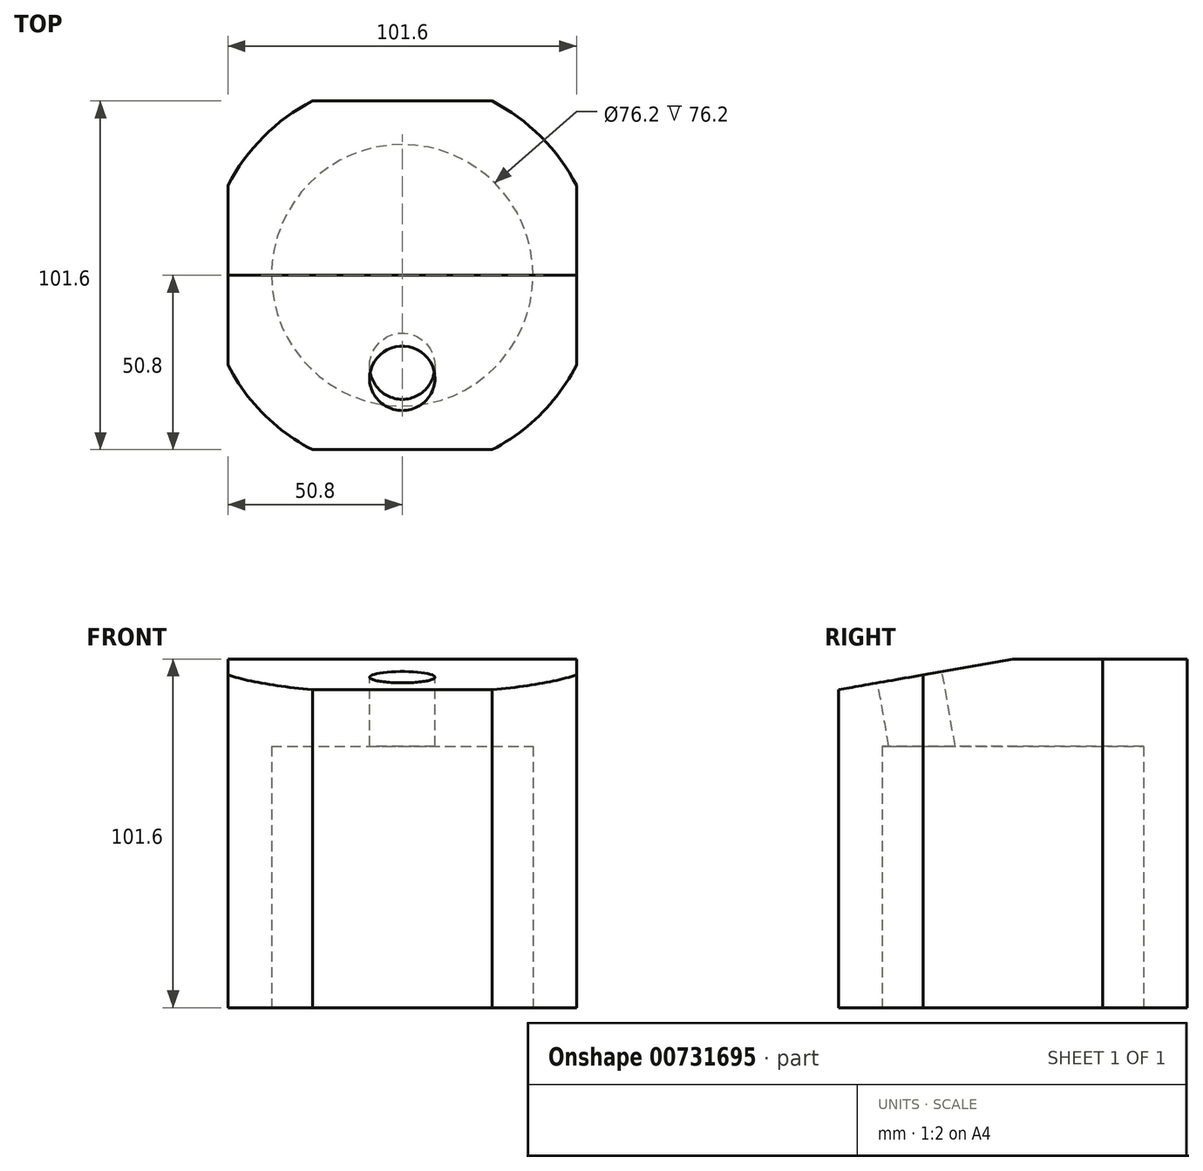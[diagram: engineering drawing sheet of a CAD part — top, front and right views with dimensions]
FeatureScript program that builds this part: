
annotation { "Feature Type Name" : "Feature", "Feature Type Description" : "" }
export const myFeature = defineFeature(function(context is Context, id is Id, definition is map)
    precondition{}
    {
        {
            var Q0;
            Q0=qCreatedBy(makeId("Top.planeOp"),FACE);
            var sketch = newSketch(context, id + "F0", { "sketchPlane" : qUnion([Q0])});
            skLineSegment(sketch, "E0.bottom", {"start": v(-50.8, 50.8) * mm, "end": v(50.8, 50.8) * mm});
            skLineSegment(sketch, "E0.top", {"start": v(-50.8, -50.8) * mm, "end": v(50.8, -50.8) * mm});
            skLineSegment(sketch, "E0.left", {"start": v(-50.8, 50.8) * mm, "end": v(-50.8, -50.8) * mm});
            skLineSegment(sketch, "E0.right", {"start": v(50.8, 50.8) * mm, "end": v(50.8, -50.8) * mm});
            skSolve(sketch);
        }
        {
            var Q0;
            Q0=makeQuery(id+"F0.imprint","IMPRINT",FACE,{"disambiguationData":[TD([[makeQuery(id+"F0.imprint","IMPRINT",EDGE,{"derivedFrom":sQuery(id+"F0.wireOp",EDGE,"E0.bottom")}),-1.0]])]});
            extrude(context, id + "F1", {"entities" : qUnion([Q0]), "endBound" : BoundingType.SYMMETRIC, "depth" : 101.6 * mm, "offsetDistance" : 25.4 * mm});
        }
        {
            var Q0;
            Q0=makeQuery(id+"F1.opExtrude","CAP_FACE",FACE,{"disambiguationData":[OSD([sQuery(id+"F0.wireOp",EDGE,"E0.bottom"),sQuery(id+"F0.wireOp",EDGE,"E0.top"),sQuery(id+"F0.wireOp",EDGE,"E0.left"),sQuery(id+"F0.wireOp",EDGE,"E0.right")])],"isStart":true});
            var sketch = newSketch(context, id + "F2", { "sketchPlane" : qUnion([Q0])});
            skCircle(sketch, "E1", {"center": v(0, 0) * mm, "radius": 38.1 * mm});
            skSolve(sketch);
        }
        {
            var Q0;
            Q0=makeQuery(id+"F2.imprint","IMPRINT",FACE,{"disambiguationData":[TD([[makeQuery(id+"F2.imprint","IMPRINT",EDGE,{"derivedFrom":sQuery(id+"F2.wireOp",EDGE,"E1")}),1.0]])]});
            extrude(context, id + "F3", {"entities" : qUnion([Q0]), "operationType" : NewBodyOperationType.REMOVE, "oppositeDirection" : true, "depth" : 76.2 * mm, "offsetDistance" : 25.4 * mm});
        }
        {
            var Q0;
            Q0=qCreatedBy(makeId("Right.planeOp"),FACE);
            var sketch = newSketch(context, id + "F4", { "sketchPlane" : qUnion([Q0])});
            skLineSegment(sketch, "E2", {"start": v(0, 50.8) * mm, "end": v(-50.8, 41.84) * mm});
            skLineSegment(sketch, "E3", {"start": v(0, 50.8) * mm, "end": v(-50.8, 50.8) * mm});
            skLineSegment(sketch, "E4", {"start": v(-50.8, 41.84) * mm, "end": v(-50.8, 50.8) * mm});
            skSolve(sketch);
        }
        {
            var Q0;
            Q0=makeQuery(id+"F4.imprint","IMPRINT",FACE,{"disambiguationData":[TD([[makeQuery(id+"F4.imprint","IMPRINT",EDGE,{"derivedFrom":sQuery(id+"F4.wireOp",EDGE,"E2")}),-1.0]])]});
            extrude(context, id + "F5", {"entities" : qUnion([Q0]), "operationType" : NewBodyOperationType.REMOVE, "endBound" : BoundingType.SYMMETRIC, "depth" : 101.6 * mm, "offsetDistance" : 25.4 * mm});
        }
        {
            var Q0;
            Q0=makeQuery(id+"F5.boolean.opBoolean","COPY",FACE,{"derivedFrom":makeQuery(id+"F5.opExtrude","SWEPT_FACE",FACE,{"disambiguationData":[OSD([sQuery(id+"F4.wireOp",EDGE,"E2")])]})});
            var sketch = newSketch(context, id + "F6", { "sketchPlane" : qUnion([Q0])});
            skCircle(sketch, "E5", {"center": v(0, -21.66) * mm, "radius": 9.53 * mm});
            skSolve(sketch);
        }
        {
            var Q0;
            Q0=makeQuery(id+"F6.imprint","IMPRINT",FACE,{"disambiguationData":[TD([[makeQuery(id+"F6.imprint","IMPRINT",EDGE,{"derivedFrom":sQuery(id+"F6.wireOp",EDGE,"E5")}),1.0]])]});
            extrude(context, id + "F7", {"entities" : qUnion([Q0]), "operationType" : NewBodyOperationType.REMOVE, "oppositeDirection" : true, "depth" : 25.4 * mm, "offsetDistance" : 25.4 * mm});
        }
        {
            var Q0;
            Q0=makeQuery(id+"F1.opExtrude","CAP_FACE",FACE,{"disambiguationData":[OSD([sQuery(id+"F0.wireOp",EDGE,"E0.bottom"),sQuery(id+"F0.wireOp",EDGE,"E0.top"),sQuery(id+"F0.wireOp",EDGE,"E0.left"),sQuery(id+"F0.wireOp",EDGE,"E0.right")])],"isStart":true});
            var sketch = newSketch(context, id + "F8", { "sketchPlane" : qUnion([Q0])});
            skCircle(sketch, "E6", {"center": v(0, 0) * mm, "radius": 57.15 * mm});
            skSolve(sketch);
        }
        {
            var Q0;
            {var subQ0=sQuery(id+"F8.wireOp",EDGE,"E6");var subQ1=makeQuery(id+"F1.opExtrude","CAP_EDGE",EDGE,{"disambiguationData":[OSD([sQuery(id+"F0.wireOp",EDGE,"E0.top")])],"isStart":true});var subQ2=makeQuery(id+"F8.imprint","INTERSECT",VERTEX,{"derivedFrom":[subQ1,subQ0]});Q0=makeQuery(id+"F8.imprint","IMPRINT",FACE,{"disambiguationData":[TD([[makeQuery(id+"F8.imprint","IMPRINT",EDGE,{"disambiguationData":[TD([[subQ2,1.0]])],"derivedFrom":subQ0}),-1.0]])]});}
            var Q1;
            {var subQ0=sQuery(id+"F8.wireOp",EDGE,"E6");var subQ1=makeQuery(id+"F1.opExtrude","CAP_EDGE",EDGE,{"disambiguationData":[OSD([sQuery(id+"F0.wireOp",EDGE,"E0.top")])],"isStart":true});var subQ2=makeQuery(id+"F8.imprint","INTERSECT",VERTEX,{"derivedFrom":[subQ1,subQ0]});Q1=makeQuery(id+"F8.imprint","IMPRINT",FACE,{"disambiguationData":[TD([[makeQuery(id+"F8.imprint","IMPRINT",EDGE,{"disambiguationData":[TD([[subQ2,-1.0]])],"derivedFrom":subQ0}),-1.0]])]});}
            var Q2;
            {var subQ0=sQuery(id+"F8.wireOp",EDGE,"E6");var subQ1=makeQuery(id+"F1.opExtrude","CAP_EDGE",EDGE,{"disambiguationData":[OSD([sQuery(id+"F0.wireOp",EDGE,"E0.right")])],"isStart":true});var subQ2=makeQuery(id+"F8.imprint","INTERSECT",VERTEX,{"derivedFrom":[subQ1,subQ0]});Q2=makeQuery(id+"F8.imprint","IMPRINT",FACE,{"disambiguationData":[TD([[makeQuery(id+"F8.imprint","IMPRINT",EDGE,{"disambiguationData":[TD([[subQ2,1.0]])],"derivedFrom":subQ0}),-1.0]])]});}
            var Q3;
            {var subQ0=sQuery(id+"F8.wireOp",EDGE,"E6");var subQ1=makeQuery(id+"F1.opExtrude","CAP_EDGE",EDGE,{"disambiguationData":[OSD([sQuery(id+"F0.wireOp",EDGE,"E0.left")])],"isStart":true});var subQ2=makeQuery(id+"F8.imprint","INTERSECT",VERTEX,{"derivedFrom":[subQ1,subQ0]});Q3=makeQuery(id+"F8.imprint","IMPRINT",FACE,{"disambiguationData":[TD([[makeQuery(id+"F8.imprint","IMPRINT",EDGE,{"disambiguationData":[TD([[subQ2,-1.0]])],"derivedFrom":subQ0}),-1.0]])]});}
            extrude(context, id + "F9", {"entities" : qUnion([Q0, Q1, Q2, Q3]), "operationType" : NewBodyOperationType.REMOVE, "oppositeDirection" : true, "depth" : 127 * mm, "offsetDistance" : 25.4 * mm});
        }
    });
